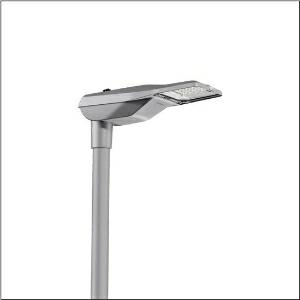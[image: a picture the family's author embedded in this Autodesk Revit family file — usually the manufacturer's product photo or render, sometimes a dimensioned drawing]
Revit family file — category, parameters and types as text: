
# Revit family: streetlight_sl_21_micro___st1_0a_5xe1d43s08db_64f0
name_source: partatom
category: Lighting Fixtures
units: mm (PartAtom-declared; Revit-internal decimal feet)

## family parameters
Cut with Voids When Loaded = No
Host = Face
Light Source = No
Part Type = Normal
Room Calculation Point = No
Round Connector Dimension = Use Diameter
Shared = No

## types (1)
- --- (1 x LED, 5320 lm, 39.1 W, 4000K)
    Apparent Load = 39 VA
    CIE Flux Codes = 37 72 97 100 100
    Color Rendering = 70
    Color Temperature = 4000K
    Default Elevation = 1800 mm
    Description = Streetlight SL 21 micro, mast luminaire, primary light control with lens, of PMMA, primary optical cover: cover, of toughened safety glass, transparent, light distribution: ST1.0a, light emission: direct distribution, primary light characteristic: asymmetric, installation type: side-entry, post-top, LED, High Power LED, rated luminous flux: 5.320lm, luminous efficacy: 136lm/W, light colour: 740, colour temperature: 4000K, control gear: D4i, control: flexible luminous flux parameterisation, time-dependent luminous flux control, constant luminous flux control, overheat protection, pre-setting: logarithmic dimming characteristic, mains connection: 220..240V, AC, 50/60Hz, start of lifetime: 39W, end of service life: 41W, reduction: 18W, luminaire housing, of diecast aluminium, powder-coated, SITECO metallic grey (DB 702S), corrosivity category C5 high according to DIN EN ISO 12944, please order mast flange separately, inclination adjustable: 0°, 5°, 10°, 15°, sealing non-destructively replaceable, multi-level sealing system, length: 528mm, width: 235mm, height: 110mm, mast flange for spigot size: 42mm (side-entry): 5XC10008XM4, 60/48mm (side-entry/post-top): 5XC10108XM2, 76/60mm (side-entry/post-top): 5XC10108XM1, Smart Interface above, protection rating (complete): IP66, insulation class (complete): insulation class II (safety insulation), certification: CE, ENEC, ENEC+, VDE, impact resistance: IK10, permissible operating ambient temperature for outdoor applications: -40..+50°C, standard-compliant lighting for roads and squares, packaging unit: 1 piece

Light Distribution: ST1.0a
    Height = 110 mm
    Lamp = 1 x LED
    Lamp Light Flux = 5320 lm
    Lamp Power = 39.1 W
    Lamp count = 1
    Length = 528 mm
    Luminous efficacy = 136 lm/W
    Manufacturer = Siteco
    ModVariant = No
    Model = 5XE1D43S08DB
    Number of Poles = 1
    OnlyDefault = Yes
    Power Factor = 1
    Product Name = Streetlight SL 21 micro | ST1.0a
    Product group = mast luminaire | pylon top
    ProductGroupID = 6100
    Protection Class = Protection class II
    Protection Degree = IP 66
    RLX_Detail_Level = 1
    RLX_Emergency_Light_Flux = 0 lm
    RLX_Emergency_Type = 0
    RLX_Emergency_Type_DB = No
    RlxData = <blob elided: 98361 chars, md5=ece749d9>
    Socket = socket
    Standby Power = 0 W
    System Light Flux = 5320 lm
    System Power = 39 W
    Type Comments = factory setting: luminous flux: 100 % | dim-lin: 254 | 765 mA
    Type Image = l_1277292.jpg
    URL = http://relux.com
    VarID = @adj_155289
    Voltage = 0 V
    Weight = 0.00 kg
    Width = 235 mm

## geometry (parser evidence)
native form markers: Blend x4, Sweep x11
no freeform markers — native parametric forms only
